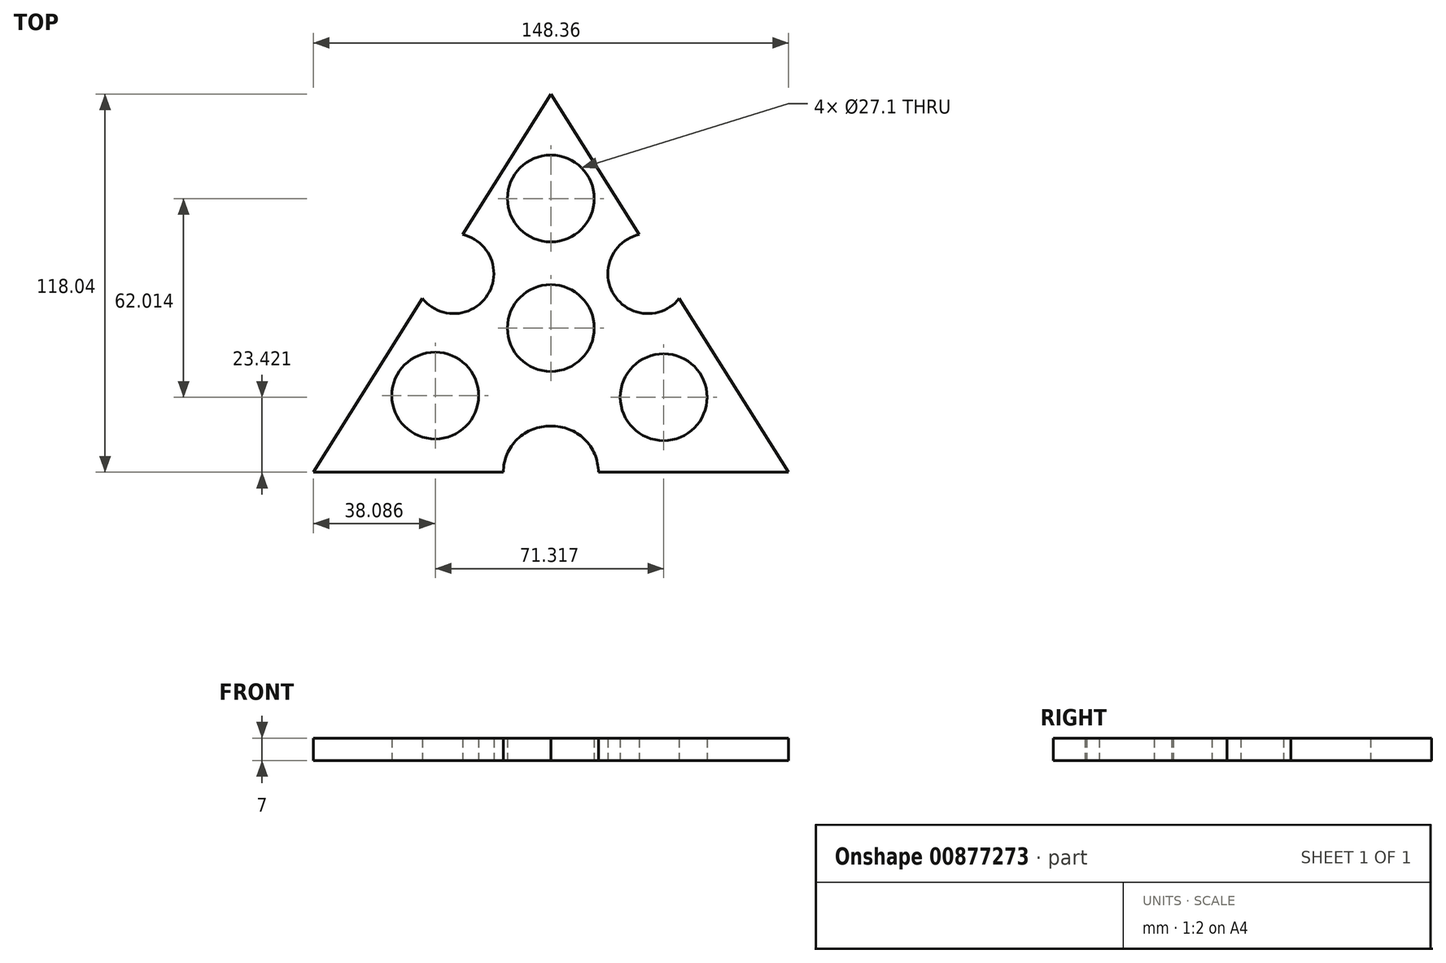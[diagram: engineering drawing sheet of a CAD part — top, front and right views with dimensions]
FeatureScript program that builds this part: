
annotation { "Feature Type Name" : "Feature", "Feature Type Description" : "" }
export const myFeature = defineFeature(function(context is Context, id is Id, definition is map)
    precondition{}
    {
        {
            var Q0;
            Q0=qCreatedBy(makeId("Top.planeOp"),FACE);
            var sketch = newSketch(context, id + "F0", { "sketchPlane" : qUnion([Q0])});
            skCircle(sketch, "E0", {"center": v(0, 0) * mm, "radius": 11.05 * mm});
            skCircle(sketch, "E1", {"center": v(0, 0) * mm, "radius": 13.55 * mm});
            skCircle(sketch, "E2", {"center": v(0, 40.43) * mm, "radius": 11.05 * mm});
            skCircle(sketch, "E3", {"center": v(0, 40.43) * mm, "radius": 13.55 * mm});
            skCircle(sketch, "E4.1.0", {"center": v(-36.1, -21.08) * mm, "radius": 11.05 * mm});
            skCircle(sketch, "E4.1.1", {"center": v(-36.1, -21.08) * mm, "radius": 13.55 * mm});
            skPoint(sketch, "E4.center", {"position": v(-0.3, -0.74) * mm});
            skCircle(sketch, "E5.1.2.0", {"center": v(35.22, -21.58) * mm, "radius": 11.05 * mm});
            skCircle(sketch, "E5.2.2.0", {"center": v(35.22, -21.58) * mm, "radius": 13.55 * mm});
            skArc(sketch, "E6", {"start": v(-40.09, 9.26) * mm, "mid": v(-19.73, 10.34) * mm, "end": v(-27.58, 29.16) * mm});
            skArc(sketch, "E7", {"start": v(0, -30.65) * mm, "mid": v(-10.47, -34.67) * mm, "end": v(-14.84, -45) * mm});
            skLineSegment(sketch, "E8", {"start": v(-74.18, -45) * mm, "end": v(-40.09, 9.26) * mm});
            skLineSegment(sketch, "E9", {"start": v(-27.58, 29.16) * mm, "end": v(0, 73.04) * mm});
            skLineSegment(sketch, "E10", {"start": v(-14.84, -45) * mm, "end": v(-74.18, -45) * mm});
            skLineSegment(sketch, "E11", {"start": v(0, 73.04) * mm, "end": v(0, -54.78) * mm});
            skArc(sketch, "E12.MirrorCS", {"start": v(40.09, 9.26) * mm, "mid": v(19.73, 10.34) * mm, "end": v(27.58, 29.16) * mm});
            skLineSegment(sketch, "E13.MirrorCS", {"start": v(74.18, -45) * mm, "end": v(40.09, 9.26) * mm});
            skLineSegment(sketch, "E14.MirrorCS", {"start": v(14.84, -45) * mm, "end": v(74.18, -45) * mm});
            skArc(sketch, "E15.MirrorCS", {"start": v(0, -30.65) * mm, "mid": v(10.47, -34.67) * mm, "end": v(14.84, -45) * mm});
            skLineSegment(sketch, "E16.MirrorCS", {"start": v(27.58, 29.16) * mm, "end": v(0, 73.04) * mm});
            skSolve(sketch);
        }
        {
            var Q0;
            Q0 = qSketchRegion(id + "F0", true);
            extrude(context, id + "F1", {"entities" : qUnion([Q0]), "depth" : 7 * mm, "offsetDistance" : 25 * mm});
        }
    });
